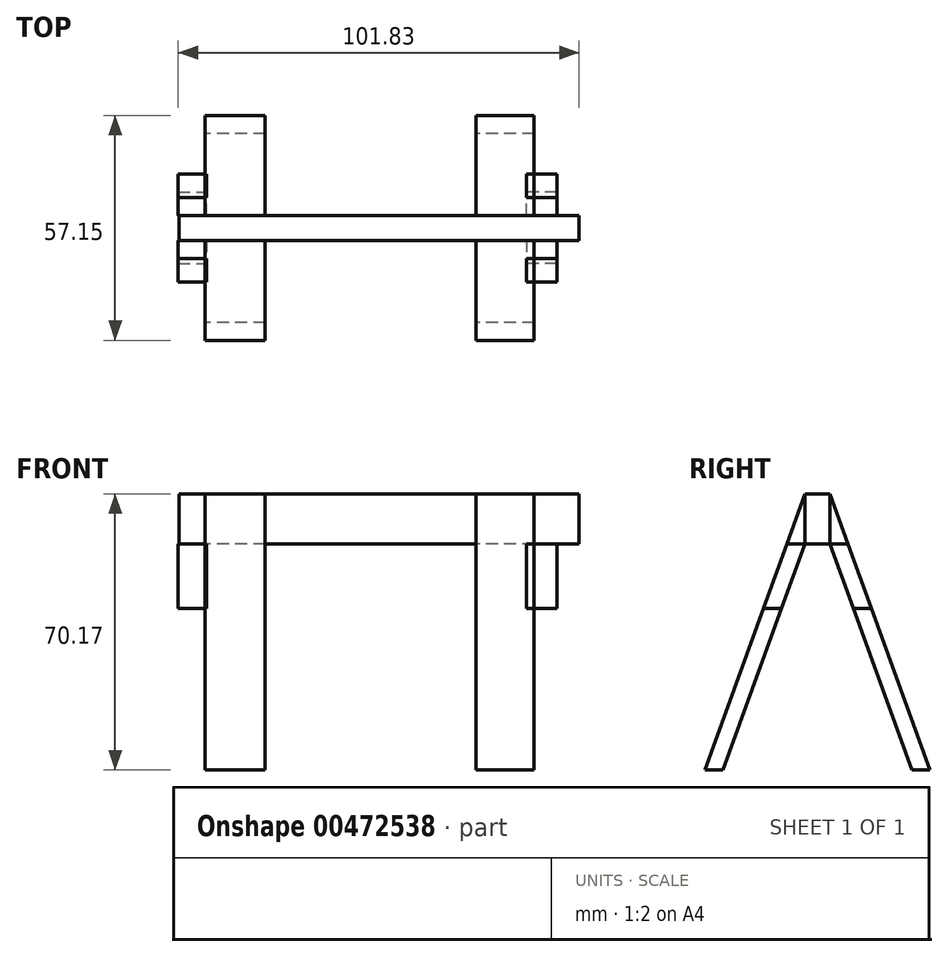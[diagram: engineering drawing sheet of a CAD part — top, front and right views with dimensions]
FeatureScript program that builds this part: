
annotation { "Feature Type Name" : "Feature", "Feature Type Description" : "" }
export const myFeature = defineFeature(function(context is Context, id is Id, definition is map)
    precondition{}
    {
        {
            var Q0;
            Q0=qCreatedBy(makeId("Right.planeOp"),FACE);
            var sketch = newSketch(context, id + "F0", { "sketchPlane" : qUnion([Q0])});
            skLineSegment(sketch, "E0.bottom", {"start": v(0, 39.76) * mm, "end": v(-6.35, 39.76) * mm});
            skLineSegment(sketch, "E0.top", {"start": v(0, 27.06) * mm, "end": v(-6.35, 27.06) * mm});
            skLineSegment(sketch, "E0.left", {"start": v(0, 39.76) * mm, "end": v(0, 27.06) * mm});
            skLineSegment(sketch, "E0.right", {"start": v(-6.35, 39.76) * mm, "end": v(-6.35, 27.06) * mm});
            skLineSegment(sketch, "E1", {"start": v(0, 39.76) * mm, "end": v(25.4, -30.4) * mm});
            skLineSegment(sketch, "E2", {"start": v(-6.35, 39.76) * mm, "end": v(-31.75, -30.4) * mm});
            skLineSegment(sketch, "E3", {"start": v(-6.35, 27.06) * mm, "end": v(-27.15, -30.4) * mm});
            skLineSegment(sketch, "E4", {"start": v(0, 27.06) * mm, "end": v(20.8, -30.4) * mm});
            skLineSegment(sketch, "E5", {"start": v(-31.75, -30.4) * mm, "end": v(-27.15, -30.4) * mm});
            skLineSegment(sketch, "E6", {"start": v(20.8, -30.4) * mm, "end": v(25.4, -30.4) * mm});
            skLineSegment(sketch, "E7", {"start": v(-16.87, 10.69) * mm, "end": v(10.52, 10.69) * mm});
            skLineSegment(sketch, "E8", {"start": v(-6.35, 27.06) * mm, "end": v(-10.95, 27.06) * mm});
            skLineSegment(sketch, "E9", {"start": v(0, 27.06) * mm, "end": v(4.6, 27.06) * mm});
            skLineSegment(sketch, "E10", {"start": v(-6.35, 27.06) * mm, "end": v(0, 27.06) * mm});
            skSolve(sketch);
        }
        {
            var Q0;
            Q0=makeQuery(id+"F0.imprint","IMPRINT",FACE,{"disambiguationData":[TD([[makeQuery(id+"F0.imprint","IMPRINT",EDGE,{"derivedFrom":sQuery(id+"F0.wireOp",EDGE,"E0.bottom")}),1.0]])]});
            extrude(context, id + "F1", {"entities" : qUnion([Q0]), "depth" : 101.6 * mm});
        }
        {
            var Q0;
            {var subQ0=sQuery(id+"F0.wireOp",EDGE,"E0.right");Q0=makeQuery(id+"F0.imprint","IMPRINT",FACE,{"disambiguationData":[TD([[makeQuery(id+"F0.imprint","IMPRINT",EDGE,{"derivedFrom":subQ0}),-1.0]])]});}
            var Q1;
            {var subQ3=sQuery(id+"F0.wireOp",EDGE,"E8");Q1=makeQuery(id+"F0.imprint","IMPRINT",FACE,{"disambiguationData":[TD([[makeQuery(id+"F0.imprint","IMPRINT",EDGE,{"derivedFrom":subQ3}),1.0]])]});}
            var Q2;
            {var subQ0=sQuery(id+"F0.wireOp",EDGE,"E0.left");Q2=makeQuery(id+"F0.imprint","IMPRINT",FACE,{"disambiguationData":[TD([[makeQuery(id+"F0.imprint","IMPRINT",EDGE,{"derivedFrom":subQ0}),1.0]])]});}
            var Q3;
            {var subQ3=sQuery(id+"F0.wireOp",EDGE,"E9");Q3=makeQuery(id+"F0.imprint","IMPRINT",FACE,{"disambiguationData":[TD([[makeQuery(id+"F0.imprint","IMPRINT",EDGE,{"derivedFrom":subQ3}),-1.0]])]});}
            var Q4;
            {var subQ0=sQuery(id+"F0.wireOp",EDGE,"E5");Q4=makeQuery(id+"F0.imprint","IMPRINT",FACE,{"disambiguationData":[TD([[makeQuery(id+"F0.imprint","IMPRINT",EDGE,{"derivedFrom":subQ0}),1.0]])]});}
            var Q5;
            {var subQ0=sQuery(id+"F0.wireOp",EDGE,"E6");Q5=makeQuery(id+"F0.imprint","IMPRINT",FACE,{"disambiguationData":[TD([[makeQuery(id+"F0.imprint","IMPRINT",EDGE,{"derivedFrom":subQ0}),1.0]])]});}
            extrude(context, id + "F2", {"entities" : qUnion([Q0, Q1, Q2, Q3, Q4, Q5]), "operationType" : NewBodyOperationType.ADD, "depth" : 20.83 * mm, "hasSecondDirection" : true, "secondDirectionOppositeDirection" : false, "secondDirectionDepth" : 6.6 * mm});
        }
        {
            var Q0;
            {var subQ0=sQuery(id+"F0.wireOp",EDGE,"E6");Q0=makeQuery(id+"F0.imprint","IMPRINT",FACE,{"disambiguationData":[TD([[makeQuery(id+"F0.imprint","IMPRINT",EDGE,{"derivedFrom":subQ0}),1.0]])]});}
            var Q1;
            {var subQ3=sQuery(id+"F0.wireOp",EDGE,"E9");Q1=makeQuery(id+"F0.imprint","IMPRINT",FACE,{"disambiguationData":[TD([[makeQuery(id+"F0.imprint","IMPRINT",EDGE,{"derivedFrom":subQ3}),-1.0]])]});}
            var Q2;
            {var subQ3=sQuery(id+"F0.wireOp",EDGE,"E8");Q2=makeQuery(id+"F0.imprint","IMPRINT",FACE,{"disambiguationData":[TD([[makeQuery(id+"F0.imprint","IMPRINT",EDGE,{"derivedFrom":subQ3}),1.0]])]});}
            var Q3;
            {var subQ0=sQuery(id+"F0.wireOp",EDGE,"E0.right");Q3=makeQuery(id+"F0.imprint","IMPRINT",FACE,{"disambiguationData":[TD([[makeQuery(id+"F0.imprint","IMPRINT",EDGE,{"derivedFrom":subQ0}),-1.0]])]});}
            var Q4;
            {var subQ0=sQuery(id+"F0.wireOp",EDGE,"E0.left");Q4=makeQuery(id+"F0.imprint","IMPRINT",FACE,{"disambiguationData":[TD([[makeQuery(id+"F0.imprint","IMPRINT",EDGE,{"derivedFrom":subQ0}),1.0]])]});}
            var Q5;
            {var subQ0=sQuery(id+"F0.wireOp",EDGE,"E5");Q5=makeQuery(id+"F0.imprint","IMPRINT",FACE,{"disambiguationData":[TD([[makeQuery(id+"F0.imprint","IMPRINT",EDGE,{"derivedFrom":subQ0}),1.0]])]});}
            extrude(context, id + "F3", {"entities" : qUnion([Q0, Q1, Q2, Q3, Q4, Q5]), "operationType" : NewBodyOperationType.ADD, "depth" : 90.17 * mm, "hasSecondDirection" : true, "secondDirectionOppositeDirection" : false, "secondDirectionDepth" : 75.44 * mm});
        }
        {
            var Q0;
            {var subQ0=sQuery(id+"F0.wireOp",EDGE,"E6");Q0=makeQuery(id+"F0.imprint","IMPRINT",FACE,{"disambiguationData":[TD([[makeQuery(id+"F0.imprint","IMPRINT",EDGE,{"derivedFrom":subQ0}),1.0]])]});}
            var Q1;
            {var subQ0=sQuery(id+"F0.wireOp",EDGE,"E5");Q1=makeQuery(id+"F0.imprint","IMPRINT",FACE,{"disambiguationData":[TD([[makeQuery(id+"F0.imprint","IMPRINT",EDGE,{"derivedFrom":subQ0}),1.0]])]});}
            var Q2;
            {var subQ0=sQuery(id+"F0.wireOp",EDGE,"E0.left");Q2=makeQuery(id+"F0.imprint","IMPRINT",FACE,{"disambiguationData":[TD([[makeQuery(id+"F0.imprint","IMPRINT",EDGE,{"derivedFrom":subQ0}),1.0]])]});}
            var Q3;
            {var subQ0=sQuery(id+"F0.wireOp",EDGE,"E0.right");Q3=makeQuery(id+"F0.imprint","IMPRINT",FACE,{"disambiguationData":[TD([[makeQuery(id+"F0.imprint","IMPRINT",EDGE,{"derivedFrom":subQ0}),-1.0]])]});}
            var Q4;
            Q4=makeQuery(id+"F0.imprint","IMPRINT",FACE,{"disambiguationData":[TD([[makeQuery(id+"F0.imprint","IMPRINT",EDGE,{"derivedFrom":sQuery(id+"F0.wireOp",EDGE,"E0.bottom")}),1.0]])]});
            var Q5;
            {var subQ3=sQuery(id+"F0.wireOp",EDGE,"E9");Q5=makeQuery(id+"F0.imprint","IMPRINT",FACE,{"disambiguationData":[TD([[makeQuery(id+"F0.imprint","IMPRINT",EDGE,{"derivedFrom":subQ3}),-1.0]])]});}
            var Q6;
            {var subQ3=sQuery(id+"F0.wireOp",EDGE,"E8");Q6=makeQuery(id+"F0.imprint","IMPRINT",FACE,{"disambiguationData":[TD([[makeQuery(id+"F0.imprint","IMPRINT",EDGE,{"derivedFrom":subQ3}),1.0]])]});}
            extrude(context, id + "F4", {"entities" : qUnion([Q0, Q1, Q2, Q3, Q4, Q5, Q6]), "operationType" : NewBodyOperationType.ADD, "depth" : 21.84 * mm, "hasSecondDirection" : true, "secondDirectionOppositeDirection" : false, "secondDirectionDepth" : 6.6 * mm});
        }
        {
            var Q0;
            {var subQ3=sQuery(id+"F0.wireOp",EDGE,"E9");Q0=makeQuery(id+"F0.imprint","IMPRINT",FACE,{"disambiguationData":[TD([[makeQuery(id+"F0.imprint","IMPRINT",EDGE,{"derivedFrom":subQ3}),-1.0]])]});}
            var Q1;
            {var subQ0=sQuery(id+"F0.wireOp",EDGE,"E10");Q1=makeQuery(id+"F0.imprint","IMPRINT",FACE,{"disambiguationData":[TD([[makeQuery(id+"F0.imprint","IMPRINT",EDGE,{"derivedFrom":subQ0}),-1.0]])]});}
            var Q2;
            {var subQ3=sQuery(id+"F0.wireOp",EDGE,"E8");Q2=makeQuery(id+"F0.imprint","IMPRINT",FACE,{"disambiguationData":[TD([[makeQuery(id+"F0.imprint","IMPRINT",EDGE,{"derivedFrom":subQ3}),1.0]])]});}
            extrude(context, id + "F5", {"entities" : qUnion([Q0, Q1, Q2]), "oppositeDirection" : true, "depth" : 0.23 * mm, "hasSecondDirection" : true, "secondDirectionOppositeDirection" : false, "secondDirectionDepth" : 6.96 * mm});
        }
        {
            var Q0;
            {var subQ3=sQuery(id+"F0.wireOp",EDGE,"E9");Q0=makeQuery(id+"F0.imprint","IMPRINT",FACE,{"disambiguationData":[TD([[makeQuery(id+"F0.imprint","IMPRINT",EDGE,{"derivedFrom":subQ3}),-1.0]])]});}
            var Q1;
            {var subQ3=sQuery(id+"F0.wireOp",EDGE,"E8");Q1=makeQuery(id+"F0.imprint","IMPRINT",FACE,{"disambiguationData":[TD([[makeQuery(id+"F0.imprint","IMPRINT",EDGE,{"derivedFrom":subQ3}),1.0]])]});}
            var Q2;
            {var subQ0=sQuery(id+"F0.wireOp",EDGE,"E10");Q2=makeQuery(id+"F0.imprint","IMPRINT",FACE,{"disambiguationData":[TD([[makeQuery(id+"F0.imprint","IMPRINT",EDGE,{"derivedFrom":subQ0}),-1.0]])]});}
            extrude(context, id + "F6", {"entities" : qUnion([Q0, Q1, Q2]), "depth" : 95.96 * mm, "hasSecondDirection" : true, "secondDirectionOppositeDirection" : false, "secondDirectionDepth" : 88.2 * mm});
        }
    });
